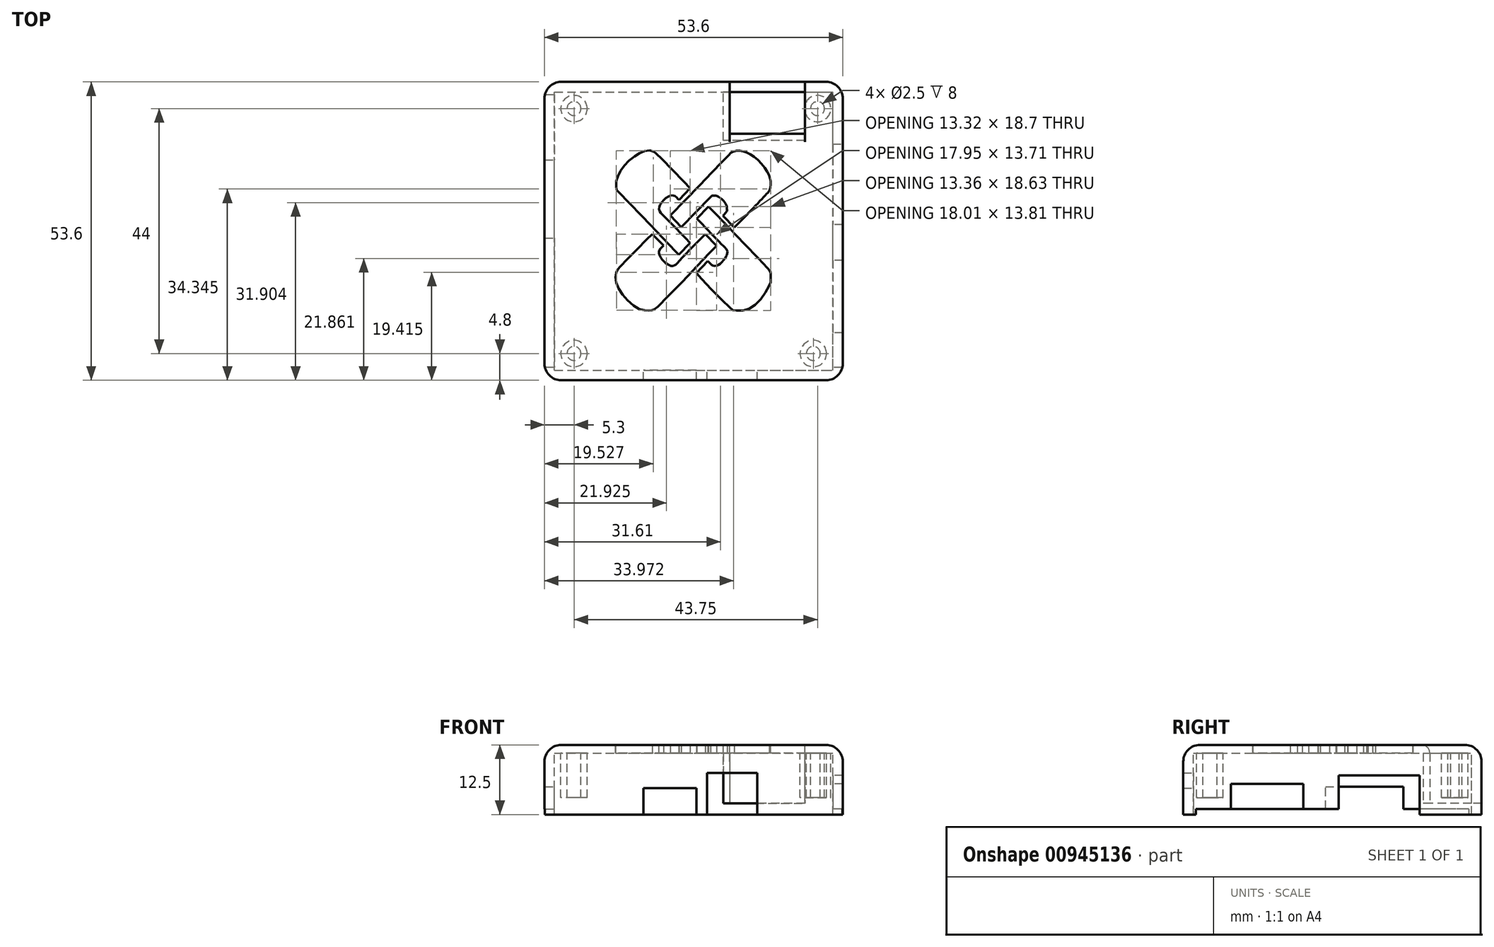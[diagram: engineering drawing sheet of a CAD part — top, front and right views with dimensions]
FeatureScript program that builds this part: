
annotation { "Feature Type Name" : "Feature", "Feature Type Description" : "" }
export const myFeature = defineFeature(function(context is Context, id is Id, definition is map)
    precondition{}
    {
        {
            var Q0;
            Q0=qCreatedBy(makeId("Top.planeOp"),FACE);
            var sketch = newSketch(context, id + "F0", { "sketchPlane" : qUnion([Q0])});
            skPoint(sketch, "E0.middle", {"position": v(0, 0) * mm});
            skLineSegment(sketch, "E1.bottom", {"start": v(-25, -25) * mm, "end": v(25, -25) * mm});
            skLineSegment(sketch, "E1.top", {"start": v(-25, 25) * mm, "end": v(25, 25) * mm});
            skLineSegment(sketch, "E1.left", {"start": v(-25, -25) * mm, "end": v(-25, 25) * mm});
            skLineSegment(sketch, "E1.right", {"start": v(25, -25) * mm, "end": v(25, 25) * mm});
            skLineSegment(sketch, "E2.0", {"start": v(-26.8, 26.8) * mm, "end": v(26.8, 26.8) * mm});
            skLineSegment(sketch, "E2.1", {"start": v(-26.8, -26.8) * mm, "end": v(-26.8, 26.8) * mm});
            skLineSegment(sketch, "E2.2", {"start": v(-26.8, -26.8) * mm, "end": v(26.8, -26.8) * mm});
            skLineSegment(sketch, "E2.3", {"start": v(26.8, -26.8) * mm, "end": v(26.8, 26.8) * mm});
            skLineSegment(sketch, "E3.bottom", {"start": v(-21.5, -22) * mm, "end": v(21.5, -22) * mm, "construction": true});
            skLineSegment(sketch, "E3.top", {"start": v(-21.5, 22) * mm, "end": v(21.5, 22) * mm, "construction": true});
            skLineSegment(sketch, "E3.left", {"start": v(-21.5, -22) * mm, "end": v(-21.5, 22) * mm, "construction": true});
            skLineSegment(sketch, "E3.right", {"start": v(21.5, -22) * mm, "end": v(21.5, 22) * mm, "construction": true});
            skLineSegment(sketch, "E4", {"start": v(21.5, 22) * mm, "end": v(22.25, 22) * mm, "construction": true});
            skCircle(sketch, "E5", {"center": v(22.25, 22) * mm, "radius": 1.25 * mm});
            skCircle(sketch, "E6", {"center": v(-21.5, 22) * mm, "radius": 1.25 * mm});
            skCircle(sketch, "E7", {"center": v(-21.5, -22) * mm, "radius": 1.25 * mm});
            skCircle(sketch, "E8", {"center": v(21.5, -22) * mm, "radius": 1.25 * mm});
            skCircle(sketch, "E9", {"center": v(-21.5, 22) * mm, "radius": 2.38 * mm});
            skCircle(sketch, "E10", {"center": v(22.25, 22) * mm, "radius": 2.38 * mm});
            skCircle(sketch, "E11", {"center": v(21.5, -22) * mm, "radius": 2.38 * mm});
            skCircle(sketch, "E12", {"center": v(-21.5, -22) * mm, "radius": 2.38 * mm});
            skSolve(sketch);
        }
        {
            var Q0;
            Q0=makeQuery(id+"F0.imprint","IMPRINT",FACE,{"disambiguationData":[TD([[makeQuery(id+"F0.imprint","IMPRINT",EDGE,{"derivedFrom":sQuery(id+"F0.wireOp",EDGE,"E1.bottom")}),1.0]])]});
            var Q1;
            Q1=makeQuery(id+"F0.imprint","IMPRINT",FACE,{"disambiguationData":[TD([[makeQuery(id+"F0.imprint","IMPRINT",EDGE,{"derivedFrom":sQuery(id+"F0.wireOp",EDGE,"E6")}),1.0]])]});
            var Q2;
            Q2=makeQuery(id+"F0.imprint","IMPRINT",FACE,{"disambiguationData":[TD([[makeQuery(id+"F0.imprint","IMPRINT",EDGE,{"derivedFrom":sQuery(id+"F0.wireOp",EDGE,"E5")}),1.0]])]});
            var Q3;
            Q3=makeQuery(id+"F0.imprint","IMPRINT",FACE,{"disambiguationData":[TD([[makeQuery(id+"F0.imprint","IMPRINT",EDGE,{"derivedFrom":sQuery(id+"F0.wireOp",EDGE,"E8")}),1.0]])]});
            var Q4;
            Q4=makeQuery(id+"F0.imprint","IMPRINT",FACE,{"disambiguationData":[TD([[makeQuery(id+"F0.imprint","IMPRINT",EDGE,{"derivedFrom":sQuery(id+"F0.wireOp",EDGE,"E7")}),1.0]])]});
            extrude(context, id + "F1", {"entities" : qUnion([Q0, Q1, Q2, Q3, Q4]), "depth" : 1.5 * mm});
        }
        {
            var Q0;
            Q0=makeQuery(id+"F0.imprint","IMPRINT",FACE,{"disambiguationData":[TD([[makeQuery(id+"F0.imprint","IMPRINT",EDGE,{"derivedFrom":sQuery(id+"F0.wireOp",EDGE,"E6")}),-1.0]])]});
            var Q1;
            Q1=makeQuery(id+"F0.imprint","IMPRINT",FACE,{"disambiguationData":[TD([[makeQuery(id+"F0.imprint","IMPRINT",EDGE,{"derivedFrom":sQuery(id+"F0.wireOp",EDGE,"E5")}),-1.0]])]});
            var Q2;
            Q2=makeQuery(id+"F0.imprint","IMPRINT",FACE,{"disambiguationData":[TD([[makeQuery(id+"F0.imprint","IMPRINT",EDGE,{"derivedFrom":sQuery(id+"F0.wireOp",EDGE,"E8")}),-1.0]])]});
            var Q3;
            Q3=makeQuery(id+"F0.imprint","IMPRINT",FACE,{"disambiguationData":[TD([[makeQuery(id+"F0.imprint","IMPRINT",EDGE,{"derivedFrom":sQuery(id+"F0.wireOp",EDGE,"E7")}),-1.0]])]});
            var Q4;
            Q4=makeQuery(id+"F1.opExtrude","CAP_FACE",FACE,{"disambiguationData":[OSD([sQuery(id+"F0.wireOp",EDGE,"E1.bottom"),sQuery(id+"F0.wireOp",EDGE,"E1.top"),sQuery(id+"F0.wireOp",EDGE,"E1.left"),sQuery(id+"F0.wireOp",EDGE,"E1.right"),sQuery(id+"F0.wireOp",EDGE,"E9"),sQuery(id+"F0.wireOp",EDGE,"E10"),sQuery(id+"F0.wireOp",EDGE,"E11"),sQuery(id+"F0.wireOp",EDGE,"E12")])],"isStart":false});
            extrude(context, id + "F2", {"entities" : qUnion([Q0, Q1, Q2, Q3]), "operationType" : NewBodyOperationType.ADD, "oppositeDirection" : true, "depth" : 8 * mm, "hasSecondDirection" : true, "secondDirectionOppositeDirection" : false, "secondDirectionBoundEntityFace" : qUnion([Q4]), "secondDirectionDepth" : 1.5 * mm});
        }
        {
            var Q0;
            Q0=makeQuery(id+"F0.imprint","IMPRINT",FACE,{"disambiguationData":[TD([[makeQuery(id+"F0.imprint","IMPRINT",EDGE,{"derivedFrom":sQuery(id+"F0.wireOp",EDGE,"E1.bottom")}),-1.0]])]});
            extrude(context, id + "F3", {"entities" : qUnion([Q0]), "operationType" : NewBodyOperationType.ADD, "oppositeDirection" : true, "depth" : 11 * mm, "hasSecondDirection" : true, "secondDirectionOppositeDirection" : false, "secondDirectionDepth" : 1.5 * mm});
        }
        {
            var Q0;
            Q0=qCreatedBy(makeId("Front.planeOp"),FACE);
            var sketch = newSketch(context, id + "F4", { "sketchPlane" : qUnion([Q0])});
            skLineSegment(sketch, "E13", {"start": v(0, 0) * mm, "end": v(0, -10) * mm, "construction": true});
            skLineSegment(sketch, "E14", {"start": v(0, -10) * mm, "end": v(-24.5, -10) * mm, "construction": true});
            skLineSegment(sketch, "E15", {"start": v(-24.5, -10) * mm, "end": v(-24.5, -7.25) * mm, "construction": true});
            skLineSegment(sketch, "E16", {"start": v(-24.5, -7.25) * mm, "end": v(-4.25, -7.25) * mm, "construction": true});
            skLineSegment(sketch, "E17.bottom", {"start": v(-9, -8.25) * mm, "end": v(0.5, -8.25) * mm});
            skLineSegment(sketch, "E17.top", {"start": v(-9, -6.25) * mm, "end": v(0.5, -6.25) * mm});
            skLineSegment(sketch, "E17.left", {"start": v(-9, -8.25) * mm, "end": v(-9, -6.25) * mm});
            skLineSegment(sketch, "E17.right", {"start": v(0.5, -8.25) * mm, "end": v(0.5, -6.25) * mm});
            skPoint(sketch, "E17.middle", {"position": v(-4.25, -7.25) * mm});
            skLineSegment(sketch, "E18", {"start": v(-24.5, -7.25) * mm, "end": v(-24.5, -6.15) * mm, "construction": true});
            skLineSegment(sketch, "E19", {"start": v(-24.5, -6.15) * mm, "end": v(6.9, -6.15) * mm, "construction": true});
            skLineSegment(sketch, "E20.bottom", {"start": v(11.4, -8.75) * mm, "end": v(2.4, -8.75) * mm});
            skLineSegment(sketch, "E20.top", {"start": v(11.4, -3.55) * mm, "end": v(2.4, -3.55) * mm});
            skLineSegment(sketch, "E20.left", {"start": v(11.4, -8.75) * mm, "end": v(11.4, -3.55) * mm});
            skLineSegment(sketch, "E20.right", {"start": v(2.4, -8.75) * mm, "end": v(2.4, -3.55) * mm});
            skPoint(sketch, "E20.middle", {"position": v(6.9, -6.15) * mm});
            skLineSegment(sketch, "E21", {"start": v(11.4, -8.75) * mm, "end": v(11.4, -11) * mm});
            skLineSegment(sketch, "E22", {"start": v(11.4, -11) * mm, "end": v(2.4, -11) * mm});
            skLineSegment(sketch, "E23", {"start": v(2.4, -11) * mm, "end": v(2.4, -8.75) * mm});
            skLineSegment(sketch, "E24", {"start": v(0.5, -8.25) * mm, "end": v(0.5, -11) * mm});
            skLineSegment(sketch, "E25", {"start": v(0.5, -11) * mm, "end": v(-9, -11) * mm});
            skLineSegment(sketch, "E26", {"start": v(-9, -11) * mm, "end": v(-9, -8.25) * mm});
            skLineSegment(sketch, "E27", {"start": v(2.4, -11.11) * mm, "end": v(2.4, -12.2) * mm});
            skSolve(sketch);
        }
        {
            var Q0;
            Q0=qSketchRegion(id+"F4",true);
            extrude(context, id + "F5", {"entities" : qUnion([Q0]), "operationType" : NewBodyOperationType.REMOVE, "endBound" : BoundingType.THROUGH_ALL, "depth" : 25 * mm});
        }
        {
            var Q0;
            Q0=qCreatedBy(makeId("Right.planeOp"),FACE);
            var sketch = newSketch(context, id + "F6", { "sketchPlane" : qUnion([Q0])});
            skLineSegment(sketch, "E28", {"start": v(0, 0) * mm, "end": v(0, -10) * mm, "construction": true});
            skLineSegment(sketch, "E29", {"start": v(0, -10) * mm, "end": v(-24.5, -10) * mm});
            skLineSegment(sketch, "E30", {"start": v(-24.5, -10) * mm, "end": v(-24.5, -7) * mm, "construction": true});
            skLineSegment(sketch, "E31", {"start": v(-24.5, -7) * mm, "end": v(-11.75, -7) * mm, "construction": true});
            skLineSegment(sketch, "E32.bottom", {"start": v(-18.25, -8.5) * mm, "end": v(-5.25, -8.5) * mm});
            skLineSegment(sketch, "E32.top", {"start": v(-18.25, -5.5) * mm, "end": v(-5.25, -5.5) * mm});
            skLineSegment(sketch, "E32.left", {"start": v(-18.25, -8.5) * mm, "end": v(-18.25, -5.5) * mm});
            skLineSegment(sketch, "E32.right", {"start": v(-5.25, -8.5) * mm, "end": v(-5.25, -5.5) * mm});
            skPoint(sketch, "E32.middle", {"position": v(-11.75, -7) * mm});
            skLineSegment(sketch, "E33", {"start": v(0, -10) * mm, "end": v(8.4, -10) * mm, "construction": true});
            skLineSegment(sketch, "E34", {"start": v(8.4, -10) * mm, "end": v(8.4, -7) * mm, "construction": true});
            skLineSegment(sketch, "E35.bottom", {"start": v(1.14, -10) * mm, "end": v(15.64, -10) * mm});
            skLineSegment(sketch, "E35.top", {"start": v(1.14, -4) * mm, "end": v(15.64, -4) * mm});
            skLineSegment(sketch, "E35.left", {"start": v(1.14, -10) * mm, "end": v(1.14, -4) * mm});
            skLineSegment(sketch, "E35.right", {"start": v(15.64, -10) * mm, "end": v(15.64, -4) * mm});
            skPoint(sketch, "E35.middle", {"position": v(8.4, -7) * mm});
            skLineSegment(sketch, "E36", {"start": v(-18.25, -8.5) * mm, "end": v(-18.25, -11.13) * mm});
            skLineSegment(sketch, "E37", {"start": v(-18.25, -11.13) * mm, "end": v(-5.25, -11.13) * mm});
            skLineSegment(sketch, "E38", {"start": v(-5.25, -11.13) * mm, "end": v(-5.25, -8.5) * mm});
            skLineSegment(sketch, "E39", {"start": v(1.14, -10) * mm, "end": v(1.14, -11.13) * mm});
            skLineSegment(sketch, "E40", {"start": v(1.14, -11.13) * mm, "end": v(15.64, -11.13) * mm});
            skLineSegment(sketch, "E41", {"start": v(15.64, -11.13) * mm, "end": v(15.64, -10) * mm});
            skLineSegment(sketch, "E42", {"start": v(-24.5, -10) * mm, "end": v(-24.5, -11.13) * mm});
            skLineSegment(sketch, "E43", {"start": v(-24.5, -11.13) * mm, "end": v(-18.25, -11.13) * mm});
            skLineSegment(sketch, "E44", {"start": v(0, -10) * mm, "end": v(0, -11.13) * mm});
            skLineSegment(sketch, "E45", {"start": v(0, -11.13) * mm, "end": v(-5.25, -11.13) * mm});
            skLineSegment(sketch, "E46", {"start": v(0, -10) * mm, "end": v(1.14, -10) * mm});
            skLineSegment(sketch, "E47", {"start": v(0, -11.13) * mm, "end": v(1.14, -11.13) * mm});
            skSolve(sketch);
        }
        {
            var Q0;
            Q0=qSketchRegion(id+"F6",true);
            extrude(context, id + "F7", {"entities" : qUnion([Q0]), "operationType" : NewBodyOperationType.REMOVE, "endBound" : BoundingType.THROUGH_ALL, "depth" : 25 * mm});
        }
        {
            var Q0;
            Q0=qCreatedBy(makeId("Right.planeOp"),FACE);
            cPlane(context, id + "F8", {"entities" : qUnion([Q0]), "cplaneType" : CPlaneType.OFFSET, "offset" : 6.5 * mm, "width" : 150 * mm, "height" : 150 * mm});
        }
        {
            var Q0;
            Q0=qCreatedBy(id+"F8.planeOp",FACE);
            var sketch = newSketch(context, id + "F9", { "sketchPlane" : qUnion([Q0])});
            skLineSegment(sketch, "E48", {"start": v(0, 0) * mm, "end": v(26.8, 0) * mm, "construction": true});
            skLineSegment(sketch, "E49.bottom", {"start": v(26.8, 0) * mm, "end": v(16.3, 0) * mm});
            skLineSegment(sketch, "E49.top", {"start": v(26.8, -9) * mm, "end": v(16.3, -9) * mm});
            skLineSegment(sketch, "E49.left", {"start": v(26.8, 0) * mm, "end": v(26.8, -9) * mm});
            skLineSegment(sketch, "E49.right", {"start": v(16.3, 0) * mm, "end": v(16.3, -9) * mm});
            skLineSegment(sketch, "E50.1", {"start": v(17.5, 0) * mm, "end": v(17.5, -5.8) * mm});
            skLineSegment(sketch, "E51", {"start": v(17.5, -5.8) * mm, "end": v(17.5, -9) * mm});
            skLineSegment(sketch, "E52", {"start": v(16.3, 0) * mm, "end": v(16.3, 1.5) * mm});
            skLineSegment(sketch, "E53", {"start": v(16.3, 1.5) * mm, "end": v(26.8, 1.5) * mm});
            skLineSegment(sketch, "E54", {"start": v(26.8, 1.5) * mm, "end": v(26.8, 0) * mm});
            skLineSegment(sketch, "E55", {"start": v(17.5, 0) * mm, "end": v(17.5, 1.5) * mm});
            skSolve(sketch);
        }
        {
            var Q0;
            Q0=qSketchRegion(id+"F9",true);
            extrude(context, id + "F10", {"entities" : qUnion([Q0]), "operationType" : NewBodyOperationType.REMOVE, "depth" : 13.5 * mm});
        }
        {
            var Q0;
            {var subQ0=sQuery(id+"F9.wireOp",EDGE,"E49.right");Q0=makeQuery(id+"F9.imprint","IMPRINT",FACE,{"disambiguationData":[TD([[makeQuery(id+"F9.imprint","IMPRINT",EDGE,{"derivedFrom":subQ0}),1.0]])]});}
            var Q1;
            {var subQ0=sQuery(id+"F9.wireOp",EDGE,"E52");Q1=makeQuery(id+"F9.imprint","IMPRINT",FACE,{"disambiguationData":[TD([[makeQuery(id+"F9.imprint","IMPRINT",EDGE,{"derivedFrom":subQ0}),-1.0]])]});}
            var Q2;
            Q2=makeQuery(id+"F3.opExtrude","SWEPT_FACE",FACE,{"disambiguationData":[OSD([sQuery(id+"F0.wireOp",EDGE,"E2.3")])]});
            extrude(context, id + "F11", {"entities" : qUnion([Q0, Q1]), "operationType" : NewBodyOperationType.ADD, "endBoundEntityFace" : qUnion([Q2]), "depth" : 13.5 * mm});
        }
        {
            var Q0;
            Q0=qSketchRegion(id+"F9",true);
            extrude(context, id + "F12", {"entities" : qUnion([Q0]), "operationType" : NewBodyOperationType.ADD, "oppositeDirection" : true, "depth" : 1.2 * mm});
        }
        {
            var Q0;
            {var subQ6=sQuery(id+"F0.wireOp",EDGE,"E2.3");var subQ9=sQuery(id+"F0.wireOp",EDGE,"E2.0");Q0=makeQuery(id+"F10.boolean.opBoolean","SPLIT",EDGE,{"disambiguationData":[TD([makeQuery(id+"F3.opExtrude","SWEPT_FACE",FACE,{"disambiguationData":[OSD([subQ6])]})])],"derivedFrom":makeQuery(id+"F3.opExtrude","CAP_EDGE",EDGE,{"disambiguationData":[OSD([subQ9])],"isStart":true})});}
            var Q1;
            {var subQ8=sQuery(id+"F0.wireOp",EDGE,"E2.0");var subQ13=sQuery(id+"F0.wireOp",EDGE,"E2.1");Q1=makeQuery(id+"F10.boolean.opBoolean","SPLIT",EDGE,{"disambiguationData":[TD([makeQuery(id+"F3.opExtrude","SWEPT_FACE",FACE,{"disambiguationData":[OSD([subQ13])]})])],"derivedFrom":makeQuery(id+"F3.opExtrude","CAP_EDGE",EDGE,{"disambiguationData":[OSD([subQ8])],"isStart":true})});}
            var Q2;
            {var subQ4=sQuery(id+"F9.wireOp",EDGE,"E49.right");var subQ5=sQuery(id+"F9.wireOp",EDGE,"E49.left");var subQ6=sQuery(id+"F9.wireOp",EDGE,"E49.top");var subQ7=sQuery(id+"F9.wireOp",EDGE,"E49.bottom");var subQ16=sQuery(id+"F9.wireOp",EDGE,"E50.1");Q2=makeQuery(id+"F11.boolean.opBoolean","SPLIT",EDGE,{"disambiguationData":[TD([makeQuery(id+"F10.boolean.opBoolean","COPY",FACE,{"derivedFrom":makeQuery(id+"F10.opExtrude","CAP_FACE",FACE,{"disambiguationData":[OSD([subQ7,subQ6,subQ5,subQ4])],"isStart":true})})])],"derivedFrom":makeQuery(id+"F11.opExtrude","SWEPT_EDGE",EDGE,{"disambiguationData":[OSD([subQ7,subQ16])]})});}
            var Q3;
            Q3=makeQuery(id+"F10.boolean.opBoolean","COPY",EDGE,{"derivedFrom":makeQuery(id+"F10.opExtrude","CAP_EDGE",EDGE,{"disambiguationData":[OSD([sQuery(id+"F9.wireOp",EDGE,"E49.bottom")])],"isStart":true})});
            var Q4;
            Q4=makeQuery(id+"F3.opExtrude","CAP_EDGE",EDGE,{"disambiguationData":[OSD([sQuery(id+"F0.wireOp",EDGE,"E2.1")])],"isStart":true});
            var Q5;
            Q5=makeQuery(id+"F3.opExtrude","CAP_EDGE",EDGE,{"disambiguationData":[OSD([sQuery(id+"F0.wireOp",EDGE,"E2.2")])],"isStart":true});
            var Q6;
            Q6=makeQuery(id+"F3.opExtrude","SWEPT_EDGE",EDGE,{"disambiguationData":[OSD([sQuery(id+"F0.wireOp",EDGE,"E2.1"),sQuery(id+"F0.wireOp",EDGE,"E2.2")])]});
            var Q7;
            Q7=makeQuery(id+"F10.boolean.opBoolean","COPY",EDGE,{"derivedFrom":makeQuery(id+"F10.opExtrude","CAP_EDGE",EDGE,{"disambiguationData":[OSD([sQuery(id+"F9.wireOp",EDGE,"E49.left")])],"isStart":false})});
            var Q8;
            Q8=makeQuery(id+"F3.opExtrude","SWEPT_EDGE",EDGE,{"disambiguationData":[OSD([sQuery(id+"F0.wireOp",EDGE,"E2.0"),sQuery(id+"F0.wireOp",EDGE,"E2.3")])]});
            var Q9;
            {var subQ6=sQuery(id+"F0.wireOp",EDGE,"E2.3");var subQ13=sQuery(id+"F0.wireOp",EDGE,"E2.2");Q9=makeQuery(id+"F11.boolean.opBoolean","SPLIT",EDGE,{"disambiguationData":[TD([makeQuery(id+"F3.opExtrude","SWEPT_FACE",FACE,{"disambiguationData":[OSD([subQ13])]})])],"derivedFrom":makeQuery(id+"F3.opExtrude","CAP_EDGE",EDGE,{"disambiguationData":[OSD([subQ6])],"isStart":true})});}
            var Q10;
            Q10=makeQuery(id+"F3.opExtrude","SWEPT_EDGE",EDGE,{"disambiguationData":[OSD([sQuery(id+"F0.wireOp",EDGE,"E2.2"),sQuery(id+"F0.wireOp",EDGE,"E2.3")])]});
            var Q11;
            Q11=makeQuery(id+"F3.opExtrude","SWEPT_EDGE",EDGE,{"disambiguationData":[OSD([sQuery(id+"F0.wireOp",EDGE,"E2.0"),sQuery(id+"F0.wireOp",EDGE,"E2.1")])]});
            fillet(context, id + "F13", {"entities" : qUnion([Q0, Q1, Q2, Q3, Q4, Q5, Q6, Q7, Q8, Q9, Q10, Q11]), "radius" : 3 * mm, "tangentPropagation" : true, "allowEdgeOverflow" : false});
        }
        {
            var Q0;
            Q0=makeQuery(id+"F11.opExtrude","SWEPT_EDGE",EDGE,{"disambiguationData":[OSD([sQuery(id+"F9.wireOp",EDGE,"E53"),sQuery(id+"F9.wireOp",EDGE,"E55")])]});
            fillet(context, id + "F14", {"entities" : qUnion([Q0]), "radius" : 1.5 * mm, "tangentPropagation" : true, "allowEdgeOverflow" : false});
        }
        {
            var Q0;
            Q0=qCreatedBy(makeId("Right.planeOp"),FACE);
            var sketch = newSketch(context, id + "F15", { "sketchPlane" : qUnion([Q0])});
            skLineSegment(sketch, "E56", {"start": v(0, 0) * mm, "end": v(0, -9) * mm, "construction": true});
            skLineSegment(sketch, "E57.bottom", {"start": v(24.5, -10) * mm, "end": v(-24.5, -10) * mm});
            skLineSegment(sketch, "E57.top", {"start": v(24.5, -8) * mm, "end": v(-24.5, -8) * mm});
            skLineSegment(sketch, "E57.left", {"start": v(24.5, -10) * mm, "end": v(24.5, -8) * mm});
            skLineSegment(sketch, "E57.right", {"start": v(-24.5, -10) * mm, "end": v(-24.5, -8) * mm});
            skPoint(sketch, "E57.middle", {"position": v(0, -9) * mm});
            skLineSegment(sketch, "E58", {"start": v(0, -9) * mm, "end": v(5.75, -9) * mm, "construction": true});
            skLineSegment(sketch, "E59", {"start": v(5.75, -9) * mm, "end": v(5.75, -8) * mm, "construction": true});
            skLineSegment(sketch, "E60.bottom", {"start": v(-1.25, -10) * mm, "end": v(12.75, -10) * mm});
            skLineSegment(sketch, "E60.top", {"start": v(-1.25, -6) * mm, "end": v(12.75, -6) * mm});
            skLineSegment(sketch, "E60.left", {"start": v(-1.25, -10) * mm, "end": v(-1.25, -6) * mm});
            skLineSegment(sketch, "E60.right", {"start": v(12.75, -10) * mm, "end": v(12.75, -6) * mm});
            skPoint(sketch, "E60.middle", {"position": v(5.75, -8) * mm});
            skLineSegment(sketch, "E61", {"start": v(0, -9) * mm, "end": v(-24.5, -9) * mm});
            skLineSegment(sketch, "E62", {"start": v(0, -9) * mm, "end": v(24.5, -9) * mm});
            skLineSegment(sketch, "E63", {"start": v(24.5, -10) * mm, "end": v(24.5, -11.04) * mm});
            skLineSegment(sketch, "E64", {"start": v(24.5, -11.04) * mm, "end": v(-24.5, -11.04) * mm});
            skLineSegment(sketch, "E65", {"start": v(-24.5, -11.04) * mm, "end": v(-24.5, -10) * mm});
            skSolve(sketch);
        }
        {
            var Q0;
            {var subQ5=sQuery(id+"F15.wireOp",EDGE,"E60.top");Q0=makeQuery(id+"F15.imprint","IMPRINT",FACE,{"disambiguationData":[TD([[makeQuery(id+"F15.imprint","IMPRINT",EDGE,{"derivedFrom":subQ5}),-1.0]])]});}
            var Q1;
            {var subQ1=sQuery(id+"F15.wireOp",EDGE,"E60.left");var subQ6=sQuery(id+"F15.wireOp",EDGE,"E57.top");var subQ9=makeQuery(id+"F15.imprint","INTERSECT",VERTEX,{"derivedFrom":[subQ6,subQ1]});Q1=makeQuery(id+"F15.imprint","IMPRINT",FACE,{"disambiguationData":[TD([[makeQuery(id+"F15.imprint","IMPRINT",EDGE,{"disambiguationData":[TD([[subQ9,1.0]])],"derivedFrom":subQ6}),1.0]])]});}
            var Q2;
            {var subQ1=sQuery(id+"F15.wireOp",EDGE,"E57.bottom");var subQ6=sQuery(id+"F15.wireOp",EDGE,"E60.left");var subQ9=makeQuery(id+"F15.imprint","INTERSECT",VERTEX,{"derivedFrom":[subQ1,subQ6]});Q2=makeQuery(id+"F15.imprint","IMPRINT",FACE,{"disambiguationData":[TD([[makeQuery(id+"F15.imprint","IMPRINT",EDGE,{"disambiguationData":[TD([[subQ9,1.0]])],"derivedFrom":subQ1}),-1.0]])]});}
            var Q3;
            {var subQ2=sQuery(id+"F15.wireOp",EDGE,"E63");Q3=makeQuery(id+"F15.imprint","IMPRINT",FACE,{"disambiguationData":[TD([[makeQuery(id+"F15.imprint","IMPRINT",EDGE,{"derivedFrom":subQ2}),-1.0]])]});}
            extrude(context, id + "F16", {"entities" : qUnion([Q0, Q1, Q2, Q3]), "operationType" : NewBodyOperationType.REMOVE, "endBound" : BoundingType.THROUGH_ALL, "oppositeDirection" : true, "depth" : 25 * mm});
        }
        {
            var Q0;
            Q0=qCreatedBy(makeId("Top.planeOp"),FACE);
            var sketch = newSketch(context, id + "F17", { "sketchPlane" : qUnion([Q0])});
            skLineSegment(sketch, "E66", {"start": v(-4.34, 2.65) * mm, "end": v(-2.39, 0.57) * mm});
            skLineSegment(sketch, "E67", {"start": v(-2.39, 0.57) * mm, "end": v(3.07, 6.13) * mm});
            skFitSpline(sketch, "E68", {"points": [v(3.07, 6.13) * mm, v(3.32, 6.34) * mm, v(3.67, 6.39) * mm, v(4, 6.37) * mm, v(4.45, 6.17) * mm, v(4.85, 5.91) * mm, v(5.24, 5.57) * mm, v(5.67, 5) * mm, v(5.96, 4.45) * mm, v(6, 3.91) * mm, v(5.97, 3.58) * mm, v(5.24, 2.72) * mm, v(5.18, 2.64) * mm, v(5.18, 2.58) * mm, v(5.61, 2.13) * mm, v(7.06, 0.63) * mm, v(7.16, 0.57) * mm, v(7.26, 0.62) * mm, v(13.53, 7.13) * mm, v(13.59, 7.2) * mm, v(13.6, 7.27) * mm], "startDerivative": vector(5.99, 6.43) * mm, "endDerivative": vector(1.04, 4.5) * mm});
            skFitSpline(sketch, "E69", {"points": [v(-4.34, 2.65) * mm, v(6.64, 14) * mm, v(6.71, 14.08) * mm, v(7.22, 14.32) * mm, v(8.06, 14.45) * mm, v(8.88, 14.33) * mm, v(9.67, 14.06) * mm, v(10.72, 13.42) * mm, v(12.05, 12.24) * mm, v(13.07, 10.93) * mm, v(13.56, 10.02) * mm, v(13.75, 9.3) * mm, v(13.83, 8.8) * mm, v(13.82, 7.88) * mm, v(13.59, 7.2) * mm], "startDerivative": vector(63.12, 65.17) * mm, "endDerivative": vector(-5.23, -11.69) * mm});
            skFitSpline(sketch, "E70", {"points": [v(2.42, 4.55) * mm, v(13.55, -6.99) * mm, v(13.62, -7.1) * mm, v(13.77, -7.32) * mm, v(13.84, -7.83) * mm, v(13.85, -8.83) * mm, v(13.77, -9.37) * mm, v(12.05, -12.2) * mm, v(9.1, -14.24) * mm, v(7.08, -14.22) * mm, v(6.85, -14.1) * mm, v(0.5, -7.57) * mm, v(0.43, -7.43) * mm, v(0.47, -7.3) * mm, v(2.28, -5.38) * mm, v(2.4, -5.32) * mm, v(2.5, -5.36) * mm, v(3.22, -6.08) * mm, v(3.52, -6.25) * mm, v(4.14, -6.21) * mm, v(4.55, -6) * mm, v(5.26, -5.4) * mm, v(5.8, -4.63) * mm, v(5.96, -4.32) * mm, v(6.05, -3.85) * mm, v(5.94, -3.32) * mm, v(5.24, -2.6) * mm, v(5.17, -2.53) * mm, v(0.46, 2.3) * mm, v(0.43, 2.35) * mm, v(0.4, 2.44) * mm, v(0.48, 2.55) * mm, v(2.4, 4.54) * mm, v(2.4, 4.55) * mm, v(2.42, 4.55) * mm]});
            skFitSpline(sketch, "E71", {"points": [v(2.24, -0.38) * mm, v(4.22, -2.4) * mm, v(4.25, -2.44) * mm, v(4.23, -2.5) * mm, v(4.13, -2.6) * mm, v(-6.8, -13.9) * mm, v(-7.2, -14.1) * mm, v(-7.58, -14.22) * mm, v(-8.26, -14.24) * mm, v(-9.63, -14.06) * mm, v(-12.07, -12.25) * mm, v(-13.78, -9.7) * mm, v(-14.01, -7.96) * mm, v(-13.72, -7.03) * mm, v(-12.94, -6.11) * mm, v(-7.42, -0.5) * mm, v(-7.33, -0.45) * mm, v(-7.25, -0.46) * mm, v(-7.2, -0.51) * mm, v(-5.41, -2.33) * mm, v(-5.37, -2.4) * mm, v(-5.37, -2.49) * mm, v(-5.42, -2.57) * mm, v(-6.15, -3.44) * mm, v(-6.12, -4.36) * mm, v(-5.46, -5.35) * mm, v(-4.57, -6.04) * mm, v(-3.94, -6.27) * mm, v(-3.34, -6.12) * mm, v(-2.75, -5.54) * mm, v(2.2, -0.4) * mm], "startDerivative": vector(52.2, -53.28) * mm, "endDerivative": vector(75.14, 76.72) * mm});
            skLineSegment(sketch, "E72", {"start": v(2.24, -0.38) * mm, "end": v(2.2, -0.4) * mm});
            skFitSpline(sketch, "E73", {"points": [v(-0.5, -2.34) * mm, v(-2.37, -4.27) * mm, v(-2.52, -4.32) * mm, v(-2.65, -4.25) * mm, v(-4.21, -2.62) * mm, v(-13.74, 7.27) * mm, v(-13.83, 7.37) * mm, v(-13.93, 7.9) * mm, v(-13.84, 9.22) * mm, v(-13.28, 10.58) * mm, v(-11.98, 12.3) * mm, v(-10.13, 13.75) * mm, v(-8.83, 14.38) * mm, v(-7.5, 14.42) * mm, v(-6.91, 14.1) * mm, v(-6.42, 13.64) * mm, v(-0.59, 7.67) * mm, v(-0.54, 7.62) * mm, v(-0.54, 7.57) * mm, v(-0.57, 7.51) * mm, v(-2.39, 5.6) * mm, v(-2.47, 5.53) * mm, v(-2.58, 5.55) * mm, v(-2.68, 5.63) * mm, v(-3.28, 6.22) * mm, v(-3.7, 6.39) * mm, v(-4.3, 6.33) * mm, v(-5.42, 5.52) * mm, v(-6.16, 4.4) * mm, v(-6.13, 3.6) * mm, v(-5.2, 2.53) * mm, v(-0.5, -2.3) * mm], "startDerivative": vector(-49.13, -53.12) * mm, "endDerivative": vector(71.13, -74.32) * mm});
            skLineSegment(sketch, "E74", {"start": v(-0.5, -2.3) * mm, "end": v(-0.5, -2.34) * mm});
            skLineSegment(sketch, "E75", {"start": v(-0.62, -2.18) * mm, "end": v(-2.65, -4.25) * mm});
            skLineSegment(sketch, "E76", {"start": v(-2.24, 0.73) * mm, "end": v(-4.2, 2.8) * mm});
            skLineSegment(sketch, "E77", {"start": v(2.07, -0.54) * mm, "end": v(4.1, -2.63) * mm});
            skLineSegment(sketch, "E78", {"start": v(0.56, 2.2) * mm, "end": v(2.63, 4.38) * mm});
            skLineSegment(sketch, "E79", {"start": v(2.56, -5.4) * mm, "end": v(0.5, -7.57) * mm});
            skLineSegment(sketch, "E80", {"start": v(-5.42, -2.57) * mm, "end": v(-7.45, -0.53) * mm});
            skLineSegment(sketch, "E81", {"start": v(-2.62, 5.57) * mm, "end": v(-0.61, 7.7) * mm});
            skLineSegment(sketch, "E82", {"start": v(5.24, 2.72) * mm, "end": v(7.28, 0.64) * mm});
            skSolve(sketch);
        }
        {
            var Q0;
            {var subQ0=sQuery(id+"F17.wireOp",EDGE,"E78");Q0=makeQuery(id+"F17.imprint","IMPRINT",FACE,{"disambiguationData":[TD([[makeQuery(id+"F17.imprint","IMPRINT",EDGE,{"derivedFrom":subQ0}),-1.0]])]});}
            var Q1;
            {var subQ6=sQuery(id+"F17.wireOp",EDGE,"E76");Q1=makeQuery(id+"F17.imprint","IMPRINT",FACE,{"disambiguationData":[TD([[makeQuery(id+"F17.imprint","IMPRINT",EDGE,{"derivedFrom":subQ6}),-1.0]])]});}
            var Q2;
            {var subQ0=sQuery(id+"F17.wireOp",EDGE,"E75");Q2=makeQuery(id+"F17.imprint","IMPRINT",FACE,{"disambiguationData":[TD([[makeQuery(id+"F17.imprint","IMPRINT",EDGE,{"derivedFrom":subQ0}),-1.0]])]});}
            var Q3;
            {var subQ0=sQuery(id+"F17.wireOp",EDGE,"E77");Q3=makeQuery(id+"F17.imprint","IMPRINT",FACE,{"disambiguationData":[TD([[makeQuery(id+"F17.imprint","IMPRINT",EDGE,{"derivedFrom":subQ0}),-1.0]])]});}
            extrude(context, id + "F18", {"entities" : qUnion([Q0, Q1, Q2, Q3]), "operationType" : NewBodyOperationType.REMOVE, "endBound" : BoundingType.THROUGH_ALL, "depth" : 25 * mm});
        }
        {
            var Q0;
            {var subQ0=sQuery(id+"F17.wireOp",EDGE,"E78");Q0=makeQuery(id+"F17.imprint","IMPRINT",FACE,{"disambiguationData":[TD([[makeQuery(id+"F17.imprint","IMPRINT",EDGE,{"derivedFrom":subQ0}),-1.0]])]});}
            var Q1;
            {var subQ0=sQuery(id+"F17.wireOp",EDGE,"E77");Q1=makeQuery(id+"F17.imprint","IMPRINT",FACE,{"disambiguationData":[TD([[makeQuery(id+"F17.imprint","IMPRINT",EDGE,{"derivedFrom":subQ0}),-1.0]])]});}
            var Q2;
            {var subQ0=sQuery(id+"F17.wireOp",EDGE,"E75");Q2=makeQuery(id+"F17.imprint","IMPRINT",FACE,{"disambiguationData":[TD([[makeQuery(id+"F17.imprint","IMPRINT",EDGE,{"derivedFrom":subQ0}),-1.0]])]});}
            var Q3;
            {var subQ6=sQuery(id+"F17.wireOp",EDGE,"E76");Q3=makeQuery(id+"F17.imprint","IMPRINT",FACE,{"disambiguationData":[TD([[makeQuery(id+"F17.imprint","IMPRINT",EDGE,{"derivedFrom":subQ6}),-1.0]])]});}
            extrude(context, id + "F19", {"entities" : qUnion([Q0, Q1, Q2, Q3]), "depth" : 1.5 * mm});
        }
    });
